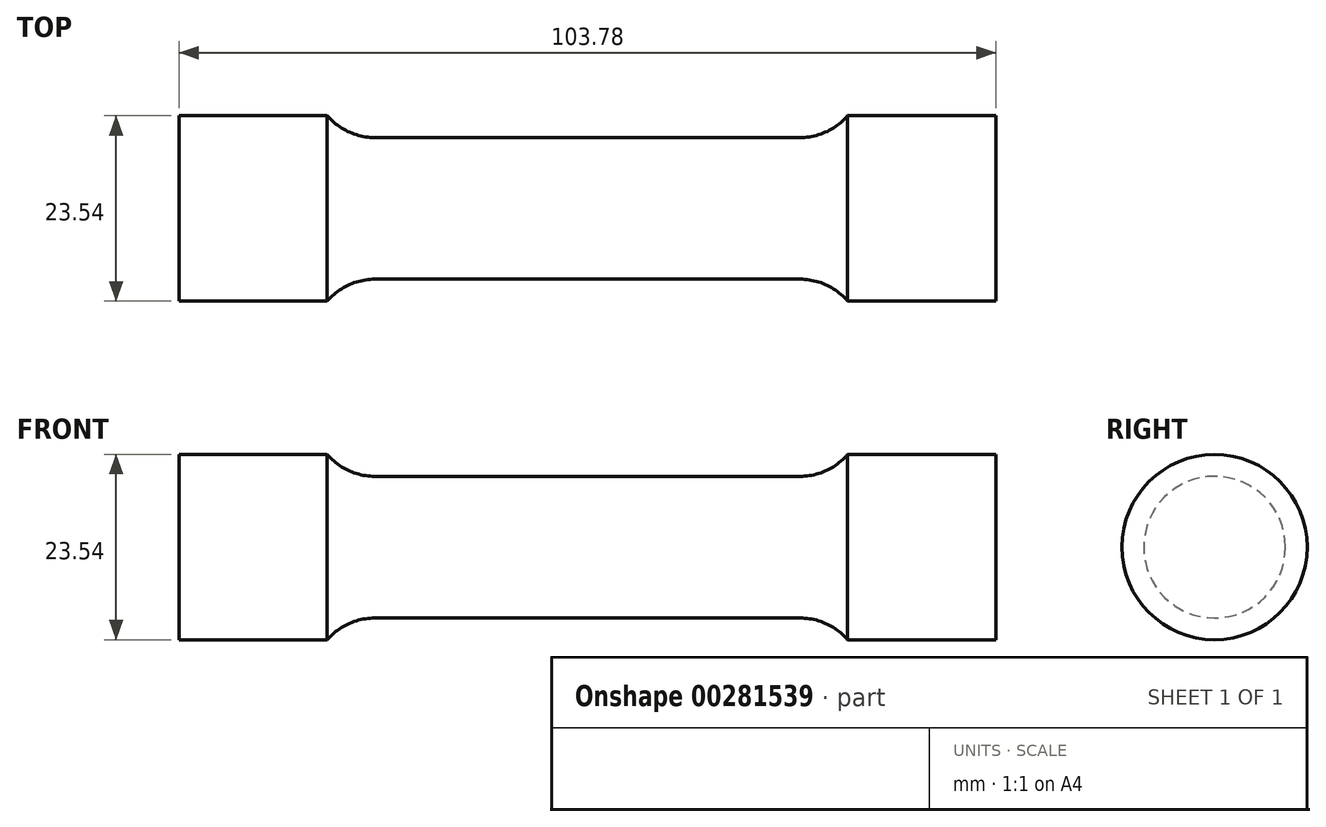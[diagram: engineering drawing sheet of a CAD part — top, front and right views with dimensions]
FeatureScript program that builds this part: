
annotation { "Feature Type Name" : "Feature", "Feature Type Description" : "" }
export const myFeature = defineFeature(function(context is Context, id is Id, definition is map)
    precondition{}
    {
        {
            var Q0;
            Q0=qCreatedBy(makeId("Front.planeOp"),FACE);
            var sketch = newSketch(context, id + "F0", { "sketchPlane" : qUnion([Q0])});
            skLineSegment(sketch, "E0", {"start": v(0, 9) * mm, "end": v(27, 9) * mm});
            skArc(sketch, "E1", {"start": v(27, 9) * mm, "mid": v(30.33, 9.72) * mm, "end": v(33.05, 11.77) * mm});
            skLineSegment(sketch, "E2", {"start": v(33.05, 11.77) * mm, "end": v(51.9, 11.77) * mm});
            skLineSegment(sketch, "E3", {"start": v(51.9, 11.77) * mm, "end": v(51.9, 0) * mm});
            skLineSegment(sketch, "E4.MirrorCS", {"start": v(-33.05, 11.77) * mm, "end": v(-51.9, 11.77) * mm});
            skLineSegment(sketch, "E5.MirrorCS", {"start": v(0, 9) * mm, "end": v(-27, 9) * mm});
            skLineSegment(sketch, "E6.MirrorCS", {"start": v(-51.9, 11.77) * mm, "end": v(-51.9, 0) * mm});
            skArc(sketch, "E7.MirrorCS", {"start": v(-27, 9) * mm, "mid": v(-30.33, 9.72) * mm, "end": v(-33.05, 11.77) * mm});
            skLineSegment(sketch, "E8", {"start": v(-51.9, 0) * mm, "end": v(51.9, 0) * mm});
            skSolve(sketch);
        }
        {
            var Q0;
            Q0 = qSketchRegion(id + "F0", true);
            var Q1;
            Q1=sQuery(id+"F0.wireOp",EDGE,"E8");
            revolve(context, id + "F1", {"entities" : qUnion([Q0]), "axis" : qUnion([Q1]), "revolveType" : RevolveType.FULL});
        }
    });
